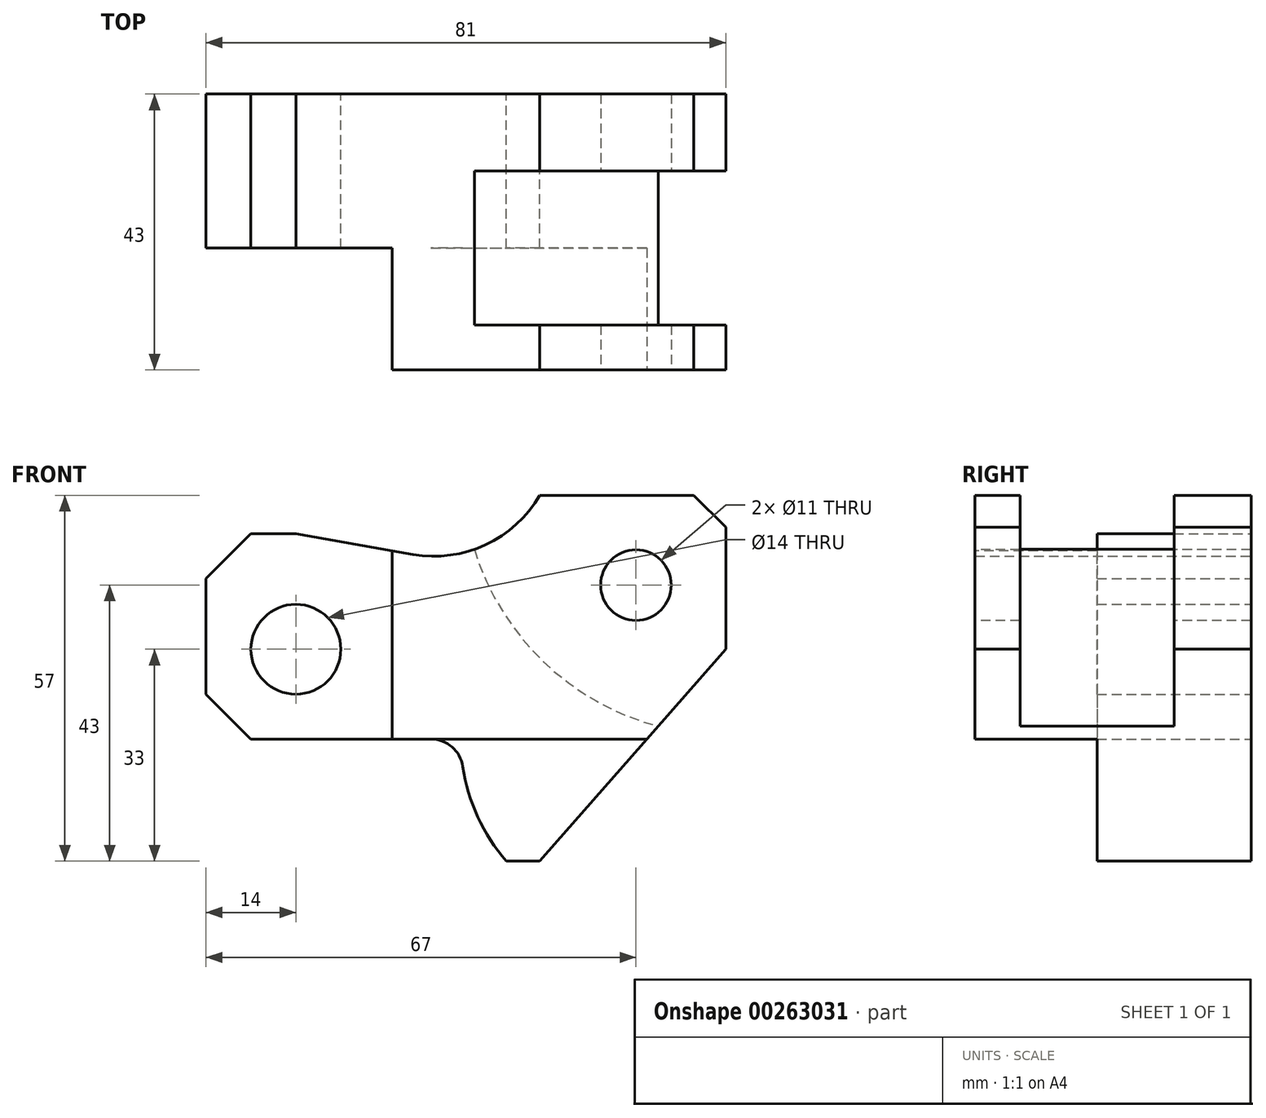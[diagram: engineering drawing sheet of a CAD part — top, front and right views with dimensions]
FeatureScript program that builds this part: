
annotation { "Feature Type Name" : "Feature", "Feature Type Description" : "" }
export const myFeature = defineFeature(function(context is Context, id is Id, definition is map)
    precondition{}
    {
        {
            var Q0;
            Q0=qCreatedBy(makeId("Front.planeOp"),FACE);
            var sketch = newSketch(context, id + "F0", { "sketchPlane" : qUnion([Q0])});
            skCircle(sketch, "E0", {"center": v(0, 0) * mm, "radius": 7 * mm});
            skLineSegment(sketch, "E1", {"start": v(-14, -7) * mm, "end": v(-14, 11) * mm});
            skLineSegment(sketch, "E2", {"start": v(-14, 11) * mm, "end": v(-7, 18) * mm});
            skLineSegment(sketch, "E3", {"start": v(-7, 18) * mm, "end": v(0, 18) * mm});
            skLineSegment(sketch, "E4", {"start": v(-14, -7) * mm, "end": v(-7, -14) * mm});
            skLineSegment(sketch, "E5", {"start": v(67, 0) * mm, "end": v(67, 19) * mm});
            skLineSegment(sketch, "E6", {"start": v(62, 24) * mm, "end": v(67, 19) * mm});
            skLineSegment(sketch, "E7", {"start": v(62, 24) * mm, "end": v(38, 24) * mm});
            skArc(sketch, "E8", {"start": v(38, 24) * mm, "mid": v(29.57, 16.28) * mm, "end": v(18.24, 14.78) * mm});
            skLineSegment(sketch, "E9", {"start": v(0, 18) * mm, "end": v(18.24, 14.78) * mm});
            skLineSegment(sketch, "E10", {"start": v(67, 0) * mm, "end": v(38, -33) * mm});
            skLineSegment(sketch, "E11", {"start": v(38, -33) * mm, "end": v(32.79, -33) * mm});
            skLineSegment(sketch, "E12", {"start": v(-7, -14) * mm, "end": v(21.07, -14) * mm});
            skLineSegment(sketch, "E13", {"start": v(21.07, -14) * mm, "end": v(54.7, -14) * mm, "construction": true});
            skArc(sketch, "E14", {"start": v(32.79, -33) * mm, "mid": v(28.35, -26.12) * mm, "end": v(26.01, -18.26) * mm});
            skArc(sketch, "E15", {"start": v(21.07, -14) * mm, "mid": v(24.33, -15.21) * mm, "end": v(26.01, -18.26) * mm});
            skSolve(sketch);
        }
        {
            var Q0;
            Q0 = qSketchRegion(id + "F0", true);
            extrude(context, id + "F1", {"entities" : qUnion([Q0]), "endBound" : BoundingType.SYMMETRIC, "depth" : 43 * mm});
        }
        {
            var Q0;
            Q0=makeQuery(id+"F1.opExtrude","CAP_FACE",FACE,{"disambiguationData":[OSD([sQuery(id+"F0.wireOp",EDGE,"E0"),sQuery(id+"F0.wireOp",EDGE,"E1"),sQuery(id+"F0.wireOp",EDGE,"E2"),sQuery(id+"F0.wireOp",EDGE,"E3"),sQuery(id+"F0.wireOp",EDGE,"E4"),sQuery(id+"F0.wireOp",EDGE,"E5"),sQuery(id+"F0.wireOp",EDGE,"E6"),sQuery(id+"F0.wireOp",EDGE,"E7"),sQuery(id+"F0.wireOp",EDGE,"E8"),sQuery(id+"F0.wireOp",EDGE,"E9"),sQuery(id+"F0.wireOp",EDGE,"E10"),sQuery(id+"F0.wireOp",EDGE,"E11"),sQuery(id+"F0.wireOp",EDGE,"E12"),sQuery(id+"F0.wireOp",EDGE,"E14"),sQuery(id+"F0.wireOp",EDGE,"E15")])],"isStart":false});
            var sketch = newSketch(context, id + "F2", { "sketchPlane" : qUnion([Q0])});
            skCircle(sketch, "E16", {"center": v(53, 10) * mm, "radius": 5.5 * mm});
            skLineSegment(sketch, "E17", {"start": v(15, 15.36) * mm, "end": v(15, -14) * mm});
            skLineSegment(sketch, "E18", {"start": v(15, -14) * mm, "end": v(54.7, -14) * mm});
            skLineSegment(sketch, "E19.0", {"start": v(0, 18) * mm, "end": v(18.24, 14.78) * mm});
            skPoint(sketch, "E20.0", {"position": v(-7, 18) * mm});
            skPoint(sketch, "E21.0", {"position": v(-14, 11) * mm});
            skPoint(sketch, "E22.0", {"position": v(-14, -7) * mm});
            skPoint(sketch, "E23.0", {"position": v(-7, -14) * mm});
            skLineSegment(sketch, "E24.0", {"start": v(-7, -14) * mm, "end": v(21.07, -14) * mm});
            skLineSegment(sketch, "E25", {"start": v(15, 15.36) * mm, "end": v(0, 18) * mm});
            skLineSegment(sketch, "E26", {"start": v(0, 18) * mm, "end": v(-7, 18) * mm});
            skLineSegment(sketch, "E27", {"start": v(-7, 18) * mm, "end": v(-14, 11) * mm});
            skLineSegment(sketch, "E28", {"start": v(-14, -7) * mm, "end": v(-7, -14) * mm});
            skPoint(sketch, "E29.0", {"position": v(38, -33) * mm});
            skPoint(sketch, "E30.0", {"position": v(32.79, -33) * mm});
            skPoint(sketch, "E31.0", {"position": v(26.01, -18.26) * mm});
            skLineSegment(sketch, "E32", {"start": v(54.7, -14) * mm, "end": v(38, -33) * mm});
            skArc(sketch, "E33", {"start": v(26.01, -18.26) * mm, "mid": v(28.35, -26.12) * mm, "end": v(32.79, -33) * mm});
            skArc(sketch, "E34", {"start": v(26.01, -18.26) * mm, "mid": v(24.33, -15.21) * mm, "end": v(21.07, -14) * mm});
            skSolve(sketch);
        }
        {
            var Q0;
            Q0 = qSketchRegion(id + "F2", true);
            extrude(context, id + "F3", {"entities" : qUnion([Q0]), "operationType" : NewBodyOperationType.REMOVE, "endBound" : BoundingType.THROUGH_ALL, "oppositeDirection" : true, "depth" : 25 * mm});
        }
        {
            var Q0;
            {var subQ2=sQuery(id+"F2.wireOp",EDGE,"E17");Q0=makeQuery(id+"F2.imprint","IMPRINT",FACE,{"disambiguationData":[TD([[makeQuery(id+"F2.imprint","IMPRINT",EDGE,{"derivedFrom":subQ2}),-1.0]])]});}
            var Q1;
            Q1=makeQuery(id+"F2.imprint","IMPRINT",FACE,{"disambiguationData":[TD([[makeQuery(id+"F2.imprint","IMPRINT",EDGE,{"derivedFrom":sQuery(id+"F2.wireOp",EDGE,"E18")}),-1.0]])]});
            extrude(context, id + "F4", {"entities" : qUnion([Q0, Q1]), "operationType" : NewBodyOperationType.REMOVE, "oppositeDirection" : true, "depth" : 19 * mm});
        }
        {
            var Q0;
            Q0=makeQuery(id+"F1.opExtrude","CAP_FACE",FACE,{"disambiguationData":[OSD([sQuery(id+"F0.wireOp",EDGE,"E0"),sQuery(id+"F0.wireOp",EDGE,"E1"),sQuery(id+"F0.wireOp",EDGE,"E2"),sQuery(id+"F0.wireOp",EDGE,"E3"),sQuery(id+"F0.wireOp",EDGE,"E4"),sQuery(id+"F0.wireOp",EDGE,"E5"),sQuery(id+"F0.wireOp",EDGE,"E6"),sQuery(id+"F0.wireOp",EDGE,"E7"),sQuery(id+"F0.wireOp",EDGE,"E8"),sQuery(id+"F0.wireOp",EDGE,"E9"),sQuery(id+"F0.wireOp",EDGE,"E10"),sQuery(id+"F0.wireOp",EDGE,"E11"),sQuery(id+"F0.wireOp",EDGE,"E12"),sQuery(id+"F0.wireOp",EDGE,"E14"),sQuery(id+"F0.wireOp",EDGE,"E15")])],"isStart":false});
            cPlane(context, id + "F5", {"entities" : qUnion([Q0]), "cplaneType" : CPlaneType.OFFSET, "offset" : 19 * mm, "oppositeDirection" : true, "width" : 150 * mm, "height" : 150 * mm});
        }
        {
            var Q0;
            Q0=qCreatedBy(id+"F5.planeOp",FACE);
            var sketch = newSketch(context, id + "F6", { "sketchPlane" : qUnion([Q0])});
            skLineSegment(sketch, "E35.0", {"start": v(62, 24) * mm, "end": v(38, 24) * mm});
            skLineSegment(sketch, "E36.0", {"start": v(67, 0) * mm, "end": v(67, 19) * mm});
            skArc(sketch, "E37.0", {"start": v(38, 24) * mm, "mid": v(29.57, 16.28) * mm, "end": v(18.24, 14.78) * mm});
            skLineSegment(sketch, "E38.0", {"start": v(67, 0) * mm, "end": v(54.7, -14) * mm});
            skArc(sketch, "E39", {"start": v(27.81, 15.56) * mm, "mid": v(38.57, -1.92) * mm, "end": v(56.45, -12) * mm});
            skLineSegment(sketch, "E40", {"start": v(56.45, -12) * mm, "end": v(67, 0) * mm});
            skLineSegment(sketch, "E41", {"start": v(67, 19) * mm, "end": v(62, 24) * mm});
            skArc(sketch, "E42", {"start": v(38, 24) * mm, "mid": v(33.67, 18.86) * mm, "end": v(27.81, 15.56) * mm});
            skCircle(sketch, "E43.0", {"center": v(53, 10) * mm, "radius": 5.5 * mm});
            skSolve(sketch);
        }
        {
            var Q0;
            Q0 = qSketchRegion(id + "F6", true);
            extrude(context, id + "F7", {"entities" : qUnion([Q0]), "operationType" : NewBodyOperationType.REMOVE, "endBound" : BoundingType.SYMMETRIC, "oppositeDirection" : true, "depth" : 24 * mm});
        }
    });
